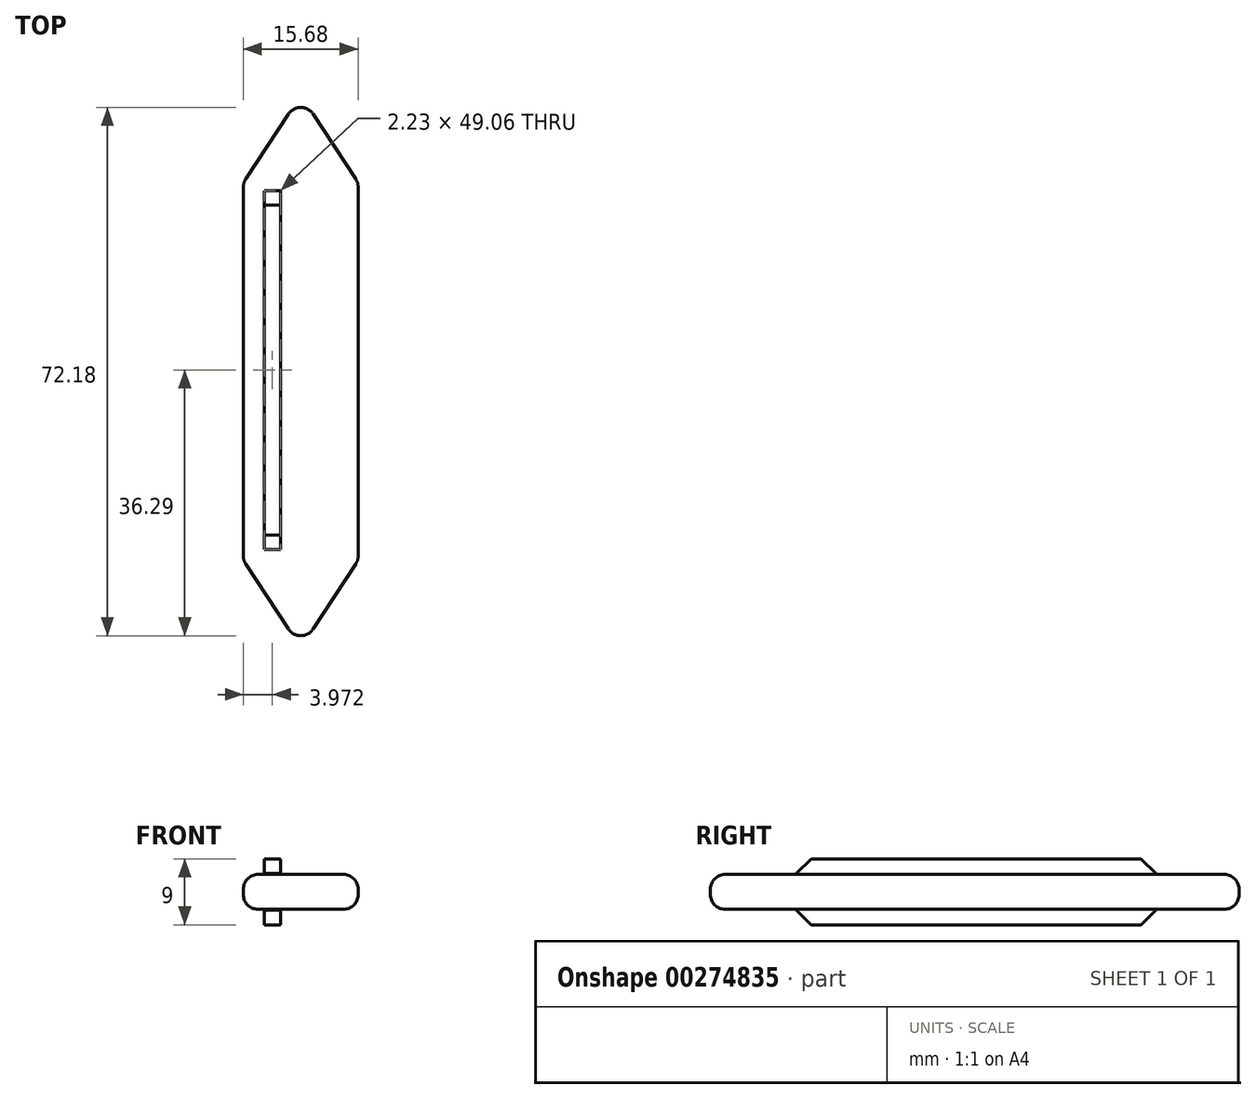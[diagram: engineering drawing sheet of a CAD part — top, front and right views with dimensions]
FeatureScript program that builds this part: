
annotation { "Feature Type Name" : "Feature", "Feature Type Description" : "" }
export const myFeature = defineFeature(function(context is Context, id is Id, definition is map)
    precondition{}
    {
        {
            var Q0;
            Q0=qCreatedBy(makeId("Top.planeOp"),FACE);
            var sketch = newSketch(context, id + "F0", { "sketchPlane" : qUnion([Q0])});
            skLineSegment(sketch, "E0", {"start": v(0, 0) * mm, "end": v(-7.84, 11.94) * mm});
            skLineSegment(sketch, "E1", {"start": v(-7.84, 11.94) * mm, "end": v(-7.84, 63.52) * mm});
            skLineSegment(sketch, "E2", {"start": v(-7.84, 63.52) * mm, "end": v(0, 75.46) * mm});
            skLineSegment(sketch, "E3", {"start": v(0, 75.46) * mm, "end": v(7.84, 63.52) * mm});
            skLineSegment(sketch, "E4", {"start": v(7.84, 63.52) * mm, "end": v(7.84, 11.94) * mm});
            skLineSegment(sketch, "E5", {"start": v(7.84, 11.94) * mm, "end": v(0, 0) * mm});
            skLineSegment(sketch, "E6.bottom", {"start": v(-4.98, 62.46) * mm, "end": v(-2.75, 62.46) * mm});
            skLineSegment(sketch, "E6.top", {"start": v(-4.98, 13.4) * mm, "end": v(-2.75, 13.4) * mm});
            skLineSegment(sketch, "E6.left", {"start": v(-4.98, 62.46) * mm, "end": v(-4.98, 13.4) * mm});
            skLineSegment(sketch, "E6.right", {"start": v(-2.75, 62.46) * mm, "end": v(-2.75, 13.4) * mm});
            skSolve(sketch);
        }
        {
            var Q0;
            Q0=makeQuery(id+"F0.imprint","IMPRINT",FACE,{"disambiguationData":[TD([[makeQuery(id+"F0.imprint","IMPRINT",EDGE,{"derivedFrom":sQuery(id+"F0.wireOp",EDGE,"E6.bottom")}),-1.0]])]});
            extrude(context, id + "F1", {"entities" : qUnion([Q0]), "endBound" : BoundingType.SYMMETRIC, "depth" : 9 * mm});
        }
        {
            var Q0;
            Q0 = qSketchRegion(id + "F0", true);
            extrude(context, id + "F2", {"entities" : qUnion([Q0]), "operationType" : NewBodyOperationType.ADD, "endBound" : BoundingType.SYMMETRIC, "depth" : 4.75 * mm});
        }
        {
            var Q0;
            Q0=makeQuery(id+"F2.opExtrude","CAP_EDGE",EDGE,{"disambiguationData":[OSD([sQuery(id+"F0.wireOp",EDGE,"E1")])],"isStart":false});
            var Q1;
            Q1=makeQuery(id+"F2.opExtrude","CAP_EDGE",EDGE,{"disambiguationData":[OSD([sQuery(id+"F0.wireOp",EDGE,"E2")])],"isStart":false});
            var Q2;
            Q2=makeQuery(id+"F2.opExtrude","CAP_EDGE",EDGE,{"disambiguationData":[OSD([sQuery(id+"F0.wireOp",EDGE,"E3")])],"isStart":false});
            var Q3;
            Q3=makeQuery(id+"F2.opExtrude","CAP_EDGE",EDGE,{"disambiguationData":[OSD([sQuery(id+"F0.wireOp",EDGE,"E4")])],"isStart":false});
            var Q4;
            Q4=makeQuery(id+"F2.opExtrude","CAP_EDGE",EDGE,{"disambiguationData":[OSD([sQuery(id+"F0.wireOp",EDGE,"E0")])],"isStart":false});
            var Q5;
            Q5=makeQuery(id+"F2.opExtrude","CAP_EDGE",EDGE,{"disambiguationData":[OSD([sQuery(id+"F0.wireOp",EDGE,"E5")])],"isStart":false});
            var Q6;
            Q6=makeQuery(id+"F2.opExtrude","CAP_EDGE",EDGE,{"disambiguationData":[OSD([sQuery(id+"F0.wireOp",EDGE,"E0")])],"isStart":true});
            var Q7;
            Q7=makeQuery(id+"F2.opExtrude","CAP_EDGE",EDGE,{"disambiguationData":[OSD([sQuery(id+"F0.wireOp",EDGE,"E1")])],"isStart":true});
            var Q8;
            Q8=makeQuery(id+"F2.opExtrude","CAP_EDGE",EDGE,{"disambiguationData":[OSD([sQuery(id+"F0.wireOp",EDGE,"E5")])],"isStart":true});
            var Q9;
            Q9=makeQuery(id+"F2.opExtrude","CAP_EDGE",EDGE,{"disambiguationData":[OSD([sQuery(id+"F0.wireOp",EDGE,"E4")])],"isStart":true});
            var Q10;
            Q10=makeQuery(id+"F2.opExtrude","CAP_EDGE",EDGE,{"disambiguationData":[OSD([sQuery(id+"F0.wireOp",EDGE,"E3")])],"isStart":true});
            var Q11;
            Q11=makeQuery(id+"F2.opExtrude","CAP_EDGE",EDGE,{"disambiguationData":[OSD([sQuery(id+"F0.wireOp",EDGE,"E2")])],"isStart":true});
            var Q12;
            Q12=makeQuery(id+"F2.opExtrude","SWEPT_EDGE",EDGE,{"disambiguationData":[OSD([sQuery(id+"F0.wireOp",EDGE,"E2"),sQuery(id+"F0.wireOp",EDGE,"E3")])]});
            var Q13;
            Q13=makeQuery(id+"F2.opExtrude","SWEPT_EDGE",EDGE,{"disambiguationData":[OSD([sQuery(id+"F0.wireOp",EDGE,"E1"),sQuery(id+"F0.wireOp",EDGE,"E2")])]});
            var Q14;
            Q14=makeQuery(id+"F2.opExtrude","SWEPT_EDGE",EDGE,{"disambiguationData":[OSD([sQuery(id+"F0.wireOp",EDGE,"E3"),sQuery(id+"F0.wireOp",EDGE,"E4")])]});
            var Q15;
            Q15=makeQuery(id+"F2.opExtrude","SWEPT_EDGE",EDGE,{"disambiguationData":[OSD([sQuery(id+"F0.wireOp",EDGE,"E4"),sQuery(id+"F0.wireOp",EDGE,"E5")])]});
            var Q16;
            Q16=makeQuery(id+"F2.opExtrude","SWEPT_EDGE",EDGE,{"disambiguationData":[OSD([sQuery(id+"F0.wireOp",EDGE,"E0"),sQuery(id+"F0.wireOp",EDGE,"E1")])]});
            var Q17;
            Q17=makeQuery(id+"F2.opExtrude","SWEPT_FACE",FACE,{"disambiguationData":[OSD([sQuery(id+"F0.wireOp",EDGE,"E0")])]});
            fillet(context, id + "F3", {"entities" : qUnion([Q0, Q1, Q2, Q3, Q4, Q5, Q6, Q7, Q8, Q9, Q10, Q11, Q12, Q13, Q14, Q15, Q16, Q17]), "radius" : 2 * mm, "tangentPropagation" : true, "allowEdgeOverflow" : false});
        }
        {
            var Q0;
            Q0=makeQuery(id+"F1.opExtrude","CAP_EDGE",EDGE,{"disambiguationData":[OSD([sQuery(id+"F0.wireOp",EDGE,"E6.bottom")])],"isStart":false});
            var Q1;
            Q1=makeQuery(id+"F1.opExtrude","CAP_EDGE",EDGE,{"disambiguationData":[OSD([sQuery(id+"F0.wireOp",EDGE,"E6.bottom")])],"isStart":true});
            var Q2;
            Q2=makeQuery(id+"F1.opExtrude","CAP_EDGE",EDGE,{"disambiguationData":[OSD([sQuery(id+"F0.wireOp",EDGE,"E6.top")])],"isStart":false});
            var Q3;
            Q3=makeQuery(id+"F1.opExtrude","CAP_EDGE",EDGE,{"disambiguationData":[OSD([sQuery(id+"F0.wireOp",EDGE,"E6.top")])],"isStart":true});
            chamfer(context, id + "F4", {"entities" : qUnion([Q0, Q1, Q2, Q3]), "width" : 2 * mm, "tangentPropagation" : true});
        }
    });
